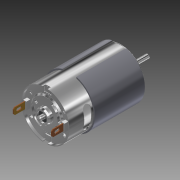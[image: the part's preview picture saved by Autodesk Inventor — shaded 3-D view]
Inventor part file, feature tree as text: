
AUTODESK INVENTOR PART (.ipt)
format: ipt  version: 2016 SP1 (Build 200210100, 210)  size: 925,184 bytes
history: native  units: mm (DEFAULTED — no unit token found)
features: extrude x24, sketch x24, fillet x7, plane x6, mirror x4, projected_geometry x3, chamfer x2, pattern_circular x2, shell x1, revolve x1
ambient origin geometry x8: Origin, YZ Plane, XZ Plane, XY Plane, X Axis, Y Axis, Z Axis, Center Point
bodies: Solid1 (feature_tree)
feature tree (74):
  extrude  "Extrusion1"  Depth=56.896mm TaperAngle=0.0deg
  fillet  "Fillet1"  Radius=2.0mm
  shell  "Shell1"  Thickness=0.62mm
  extrude  "Extrusion2"  Depth=4.572mm TaperAngle=0.0deg
  fillet  "Fillet2"  Radius=0.5mm
  plane  "Work Plane1"
  extrude  "Extrusion5"  Depth=0.62mm TaperAngle=0.0deg
  extrude  "Extrusion6"  Depth=1.016mm
  fillet  "Fillet4"  Radius=0.6096mm
  fillet  "Fillet5"  Radius=4.9276mm
  extrude  "Extrusion11"  Depth=11.43mm TaperAngle=0.0deg
  chamfer  "Chamfer1"  Distance=1.0mm
  sketch  "Sketch13"  dims[d61=3.0mm d69=18.0mm]
  mirror  "Mirror2"
  plane  "Work Plane2"
  plane  "Work Plane3"
  extrude  "Flux Ring"  Depth=18.0mm
  extrude  "Extrusion15"  Depth=1.016mm
  mirror  "Mirror3"
  sketch  "Sketch18"  dims[d83=0.254mm d93=2.413mm]
  extrude  "Extrusion16"  Depth=0.254mm
  extrude  "Extrusion17"  Depth=2.413mm
  chamfer  "Chamfer2"  Distance=2.921mm
  extrude  "Extrusion18"  Depth=3.429mm TaperAngle=0.0deg
  extrude  "Extrusion19"  Depth=3.429mm TaperAngle=0.0deg
  extrude  "Extrusion20"  Depth=1.397mm TaperAngle=0.0deg
  fillet  "Fillet9"  Radius=3.175mm
  extrude  "Extrusion21"  Depth=1.016mm
  extrude  "Extrusion22"  Depth=3.8862mm TaperAngle=0.0deg
  extrude  "Extrusion24"  Depth=0.508mm
  extrude  "Extrusion25"  Depth=1.016mm
  extrude  "Extrusion26"  Depth=3.8862mm TaperAngle=0.0deg
  plane  "Work Plane4"
  extrude  "Extrusion29"  Depth=1.860192mm
  fillet  "Fillet10"  Radius=3.699166mm
  extrude  "Extrusion30"  Depth=0.381mm
  fillet  "Fillet11"  Radius=0.6096mm
  mirror  "Mirror4"
  extrude  "Extrusion31"  Depth=1.27mm TaperAngle=0.0deg
  sketch  "Sketch29"  dims[d153=1.27mm d154=0.0mm d155=0.381mm d156=0.6096mm d157=0.0mm]
  extrude  "Extrusion32"  Depth=0.785398mm
  pattern_circular  "Circular Pattern4"  Count=40 Angle=360.0deg
  extrude  "Extrusion34"  Depth=2.949849mm
  pattern_circular  "Circular Pattern5"  [2 undecoded]
  revolve  "Revolution1"  [1 undecoded]
  extrude  "Extrusion35"  Depth=10.0076mm TaperAngle=0.0deg
  plane  "Work Plane6"
  extrude  "Extrusion36"  Depth=400.0mm TaperAngle=360.0deg
  mirror  "Mirror5"
  sketch  "Sketch1"  dims[d0=35.7886mm d1=56.896mm d2=0.0mm d3=2.0mm d4=0.62mm]
  sketch  "Sketch2"  dims[d5=13.0mm d6=4.572mm d7=0.0mm d8=0.5mm]
  sketch  "Sketch6"  dims[d30=-1.905mm d31=0.62mm d32=0.0mm]
  sketch  "Sketch7"  dims[d33=24.13mm d34=1.016mm d35=-7.853982mm d54=0.6096mm d55=4.9276mm]
  sketch  "Sketch12"  dims[d56=13.843mm d57=11.43mm d58=0.0mm d59=1.0mm d60=2.0mm]
  sketch  "Sketch15"  dims[d75=45.0deg d76=1.016mm]
  sketch  "Sketch17"  dims[d77=36.8808mm d78=0.0mm d82=0.254mm]
  sketch  "Sketch19"  dims[d95=5.588mm d96=2.921mm d97=0.0mm]
  sketch  "Sketch20"  dims[d102=25.4mm d103=0.0mm d104=3.429mm d105=0.0mm]
  sketch  "Sketch21"  dims[d106=0.508mm d107=1.27mm d108=45.0deg d109=3.429mm d110=0.0mm]
  sketch  "Sketch22"  dims[d111=3.6576mm d114=1.397mm d115=0.0mm d116=3.175mm]
  sketch  "Sketch23"  dims[d117=3.8862mm d118=77.0128mm d119=0.0mm d120=0.0mm d121=1.016mm]
  sketch  "Sketch24"  dims[d123=3.8862mm d124=0.0mm d125=3.8862mm d126=0.0mm]
  sketch  "Sketch25"  dims[d129=3.8862mm d130=0.0mm d137=0.508mm]
  projected_geometry  "Projected Loop1"
  sketch  "Sketch26"  dims[d139=0.508mm d140=1.016mm]
  projected_geometry  "Projected Loop2"
  sketch  "Sketch27"  dims[d141=0.508mm d142=3.8862mm d143=0.0mm]
  plane  "Work Plane5"
  sketch  "Sketch28"  dims[d144=0.6096mm d145=0.0mm d150=1.860192mm d152=3.699166mm]
  sketch  "Sketch30"  dims[d158=0.381mm d159=1.27mm d160=0.0mm]
  sketch  "Sketch31"  dims[d162=1.570796mm d163=0.785398mm]
  projected_geometry  "Projected Loop3"
  sketch  "Sketch32"  dims[d165=10.0076mm d166=0.0mm d167=400.0mm d168=360.0deg]
  sketch  "Sketch33"  dims[d170=3.200082mm d172=2.949849mm d173=1.570796mm d174=14.57284mm d178=10.0076mm d179=0.0mm d180=400.0mm d181=360.0deg d186=45.0deg d187=90.0deg d188=0.127mm d189=5.08mm d190=5.08mm d191=10.0076mm d192=0.0mm d193=1.27mm d194=5.715mm d195=10.668mm d196=5.334mm d197=10.0076mm d198=0.0mm]
note: 3 required parameter values undecoded (feature->parameter linkage not recoverable at this tier; creation-order binding heuristic only, values carry confidence <= 0.55)